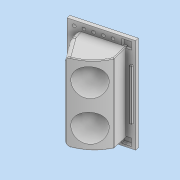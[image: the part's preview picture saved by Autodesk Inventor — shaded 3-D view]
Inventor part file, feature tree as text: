
AUTODESK INVENTOR PART (.ipt)
format: ipt  version: 2022 (Build 260153070, 153G)  size: 631,808 bytes
history: native  units: mm
features: other x6, boolean_combine x1, fillet x1
ambient origin geometry x8: Origin, YZ Plane, XZ Plane, XY Plane, X Axis, Y Axis, Z Axis, Center Point
bodies: Solid1 (feature_tree), Solid2 (feature_tree)
feature tree (8):
  other  "P00173-09-015.ipt"
  other  "P00173-09-005.ipt"
  boolean_combine  "Combine1"
  fillet  "Fillet1"  Radius=10.0mm
  other  "Solid5::P00173-09-015.ipt"
  other  "TaggingFeature1"
  other  "Solid2::P00173-09-005.ipt"
  other  "TaggingFeature2"
